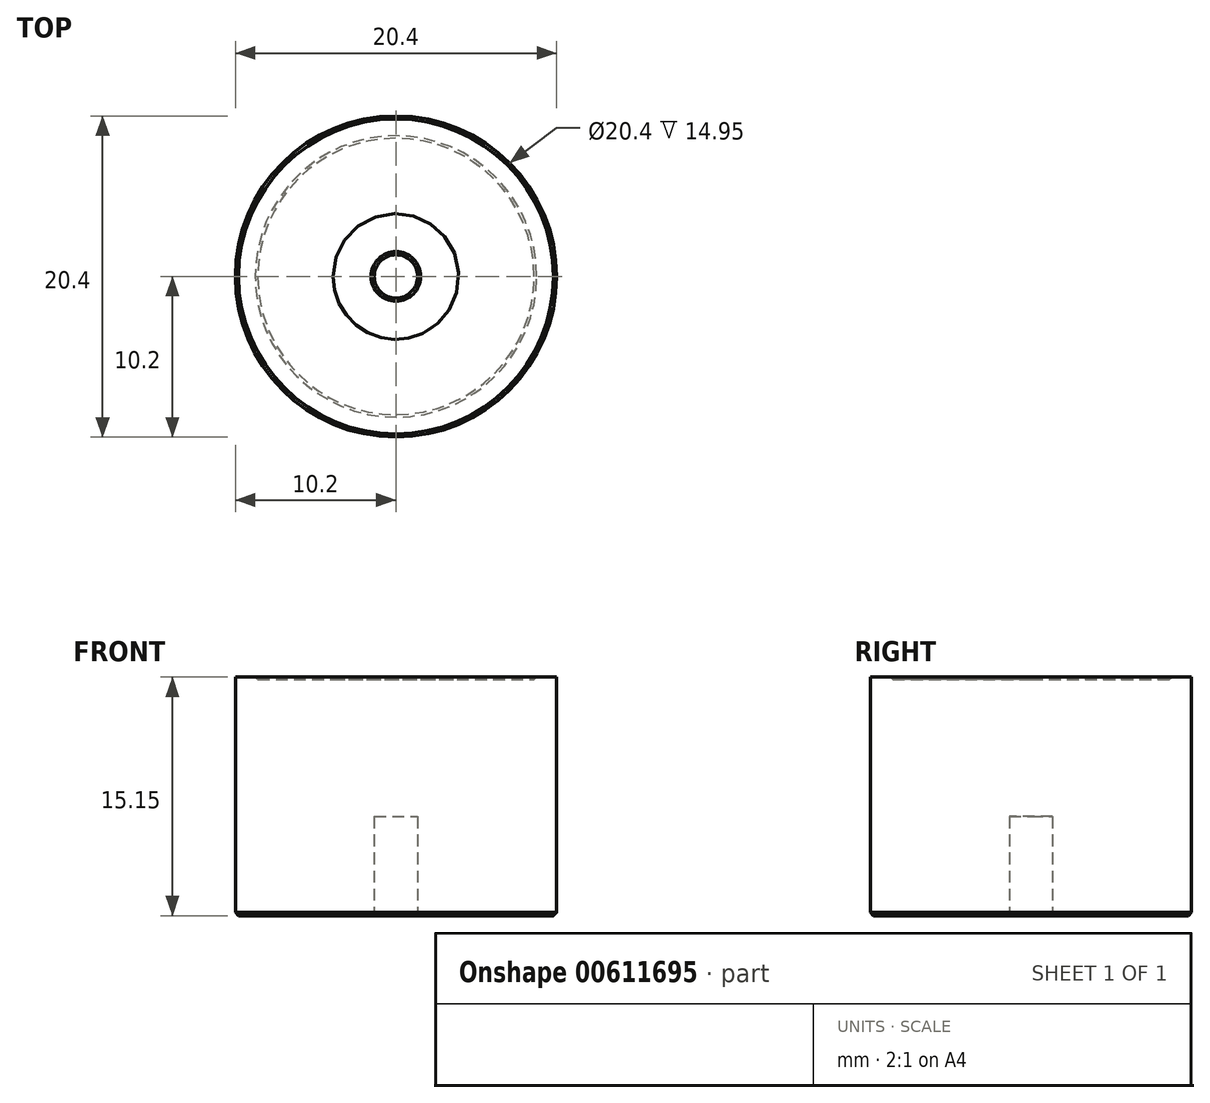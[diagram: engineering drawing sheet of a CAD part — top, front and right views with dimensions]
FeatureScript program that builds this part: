
annotation { "Feature Type Name" : "Feature", "Feature Type Description" : "" }
export const myFeature = defineFeature(function(context is Context, id is Id, definition is map)
    precondition{}
    {
        {
            var Q0;
            Q0=qCreatedBy(makeId("Front.planeOp"),FACE);
            var sketch = newSketch(context, id + "F0", { "sketchPlane" : qUnion([Q0])});
            skLineSegment(sketch, "E0.left", {"start": v(-10.2, 15.15) * mm, "end": v(-10.2, 0) * mm});
            skLineSegment(sketch, "E1", {"start": v(-8.74, 15) * mm, "end": v(-8.75, 15.15) * mm});
            skLineSegment(sketch, "E2.left", {"start": v(-4, 15.15) * mm, "end": v(-4, 15) * mm});
            skLineSegment(sketch, "E3.left", {"start": v(-1.37, 6.3) * mm, "end": v(-1.37, 0) * mm});
            skLineSegment(sketch, "E4", {"start": v(-10.2, 15.15) * mm, "end": v(-8.75, 15.15) * mm});
            skLineSegment(sketch, "E5", {"start": v(0, 15.15) * mm, "end": v(0, 6.3) * mm, "construction": true});
            skLineSegment(sketch, "E6", {"start": v(-4, 15) * mm, "end": v(-8.74, 15) * mm});
            skLineSegment(sketch, "E7", {"start": v(-10.2, 0) * mm, "end": v(-1.37, 0) * mm});
            skLineSegment(sketch, "E8", {"start": v(-4, 15.15) * mm, "end": v(0, 15.15) * mm});
            skLineSegment(sketch, "E9", {"start": v(-1.37, 6.3) * mm, "end": v(0, 6.3) * mm});
            skSolve(sketch);
        }
        {
            var Q0;
            Q0 = qSketchRegion(id + "F0", true);
            var Q1;
            Q1=sQuery(id+"F0.wireOp",EDGE,"E0.left");
            var Q2;
            Q2=sQuery(id+"F0.wireOp",EDGE,"E3.left");
            var Q3;
            Q3=sQuery(id+"F0.wireOp",EDGE,"E4");
            var Q4;
            Q4=sQuery(id+"F0.wireOp",EDGE,"E6");
            var Q5;
            Q5=sQuery(id+"F0.wireOp",EDGE,"E7");
            var Q6;
            Q6=sQuery(id+"F0.wireOp",EDGE,"E1");
            var Q7;
            Q7=sQuery(id+"F0.wireOp",EDGE,"E2.left");
            var Q8;
            Q8=sQuery(id+"F0.wireOp",EDGE,"E8");
            var Q9;
            Q9=sQuery(id+"F0.wireOp",EDGE,"E9");
            var Q10;
            Q10=sQuery(id+"F0.wireOp",EDGE,"E5");
            revolve(context, id + "F1", {"bodyType" : ToolBodyType.SURFACE, "entities" : qUnion([Q0]), "surfaceEntities" : qUnion([Q1, Q2, Q3, Q4, Q5, Q6, Q7, Q8, Q9]), "axis" : qUnion([Q10]), "revolveType" : RevolveType.FULL});
        }
        {
            var Q0;
            Q0=makeQuery(id+"F1.opRevolve","SWEPT_EDGE",EDGE,{"disambiguationData":[OSD([sQuery(id+"F0.wireOp",VERTEX,"E1.end")])]});
            var Q1;
            Q1=makeQuery(id+"F1.opRevolve","SWEPT_EDGE",EDGE,{"disambiguationData":[OSD([sQuery(id+"F0.wireOp",VERTEX,"E7.end")])]});
            var Q2;
            Q2=makeQuery(id+"F1.opRevolve","SWEPT_EDGE",EDGE,{"disambiguationData":[OSD([sQuery(id+"F0.wireOp",VERTEX,"E7.start")])]});
            chamfer(context, id + "F2", {"entities" : qUnion([Q0, Q1, Q2]), "width" : 0.2 * mm, "tangentPropagation" : true});
        }
        {
            var Q0;
            Q0=makeQuery(id+"F1.opRevolve","SWEPT_EDGE",EDGE,{"disambiguationData":[OSD([sQuery(id+"F0.wireOp",VERTEX,"E8.start")])]});
            fillet(context, id + "F3", {"entities" : qUnion([Q0]), "radius" : 0.12 * mm, "tangentPropagation" : true, "allowEdgeOverflow" : false});
        }
    });
